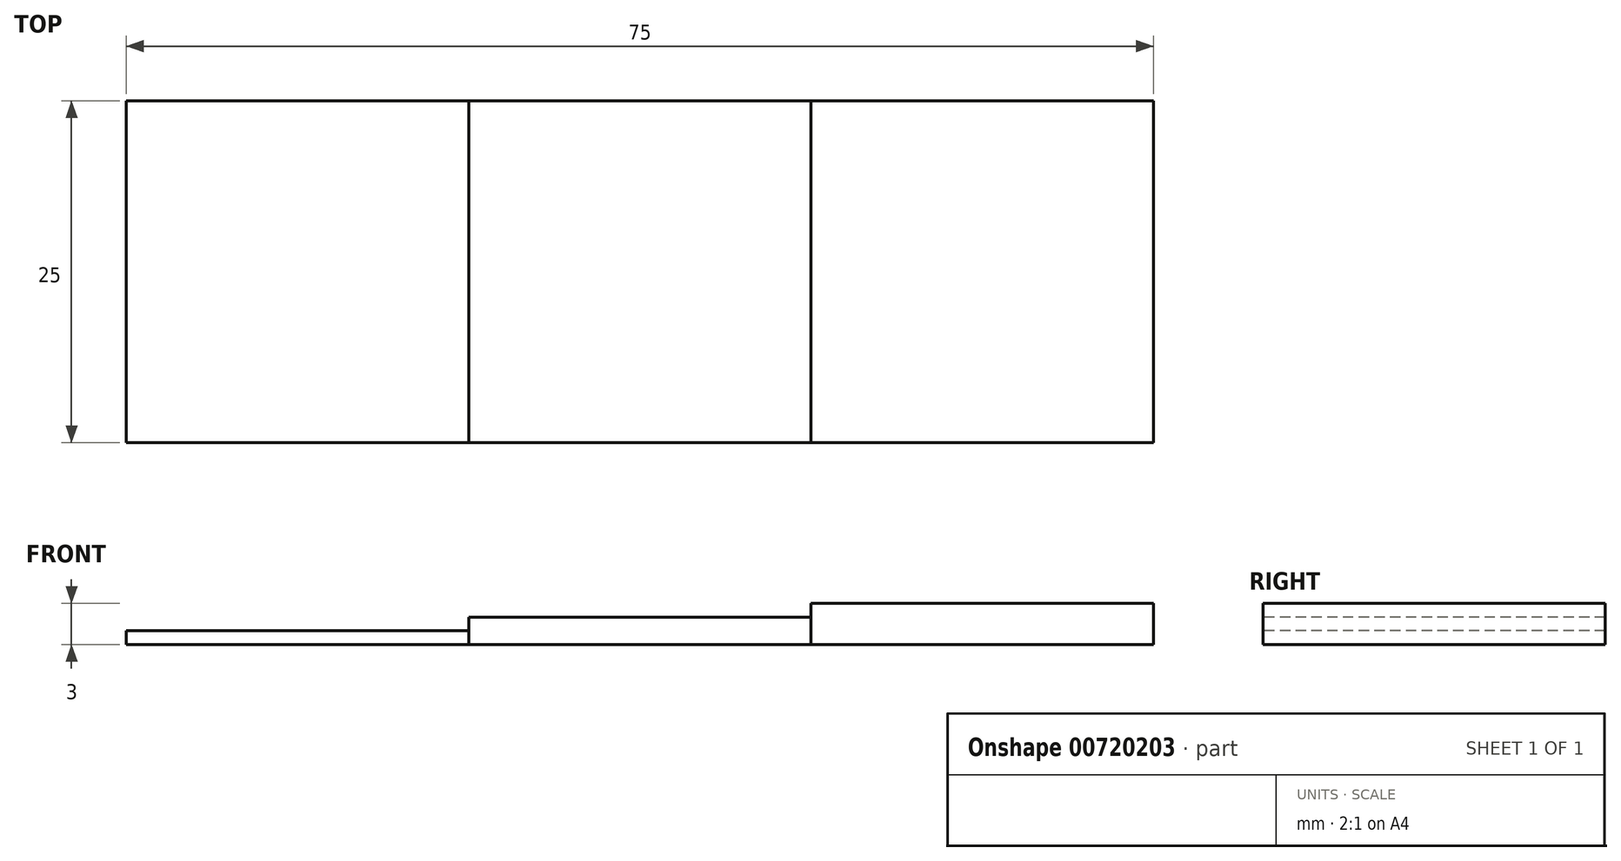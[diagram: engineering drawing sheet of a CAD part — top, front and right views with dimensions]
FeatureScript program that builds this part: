
annotation { "Feature Type Name" : "Feature", "Feature Type Description" : "" }
export const myFeature = defineFeature(function(context is Context, id is Id, definition is map)
    precondition{}
    {
        {
            var Q0;
            Q0=qCreatedBy(makeId("Top.planeOp"),FACE);
            var sketch = newSketch(context, id + "F0", { "sketchPlane" : qUnion([Q0])});
            skLineSegment(sketch, "E0.bottom", {"start": v(0, 0) * mm, "end": v(25, 0) * mm});
            skLineSegment(sketch, "E0.top", {"start": v(0, -25) * mm, "end": v(25, -25) * mm});
            skLineSegment(sketch, "E0.left", {"start": v(0, 0) * mm, "end": v(0, -25) * mm});
            skLineSegment(sketch, "E0.right", {"start": v(25, 0) * mm, "end": v(25, -25) * mm});
            skSolve(sketch);
        }
        {
            var Q0;
            Q0=makeQuery(id+"F0.imprint","IMPRINT",FACE,{"disambiguationData":[TD([[makeQuery(id+"F0.imprint","IMPRINT",EDGE,{"derivedFrom":sQuery(id+"F0.wireOp",EDGE,"E0.bottom")}),-1.0]])]});
            extrude(context, id + "F1", {"entities" : qUnion([Q0]), "depth" : 1 * mm, "offsetDistance" : 25 * mm});
        }
        {
            var Q0;
            Q0=qCreatedBy(makeId("Top.planeOp"),FACE);
            var sketch = newSketch(context, id + "F2", { "sketchPlane" : qUnion([Q0])});
            skLineSegment(sketch, "E1.bottom", {"start": v(25.05, 0) * mm, "end": v(50.05, 0) * mm});
            skLineSegment(sketch, "E1.top", {"start": v(25.05, -25) * mm, "end": v(50.05, -25) * mm});
            skLineSegment(sketch, "E1.left", {"start": v(25.05, 0) * mm, "end": v(25.05, -25) * mm});
            skLineSegment(sketch, "E1.right", {"start": v(50.05, 0) * mm, "end": v(50.05, -25) * mm});
            skSolve(sketch);
        }
        {
            var Q0;
            Q0=makeQuery(id+"F2.imprint","IMPRINT",FACE,{"disambiguationData":[TD([[makeQuery(id+"F2.imprint","IMPRINT",EDGE,{"derivedFrom":sQuery(id+"F2.wireOp",EDGE,"E1.bottom")}),-1.0]])]});
            extrude(context, id + "F3", {"entities" : qUnion([Q0]), "depth" : 2 * mm, "offsetDistance" : 25 * mm});
        }
        {
            var Q0;
            Q0=makeQuery(id+"F3.opExtrude","CAP_FACE",FACE,{"disambiguationData":[OSD([sQuery(id+"F2.wireOp",EDGE,"E1.bottom"),sQuery(id+"F2.wireOp",EDGE,"E1.top"),sQuery(id+"F2.wireOp",EDGE,"E1.left"),sQuery(id+"F2.wireOp",EDGE,"E1.right")])],"isStart":false});
            var sketch = newSketch(context, id + "F4", { "sketchPlane" : qUnion([Q0])});
            skLineSegment(sketch, "E2.bottom", {"start": v(50.05, 0) * mm, "end": v(75.05, 0) * mm});
            skLineSegment(sketch, "E2.top", {"start": v(50.05, -25) * mm, "end": v(75.05, -25) * mm});
            skLineSegment(sketch, "E2.left", {"start": v(50.05, 0) * mm, "end": v(50.05, -25) * mm});
            skLineSegment(sketch, "E2.right", {"start": v(75.05, 0) * mm, "end": v(75.05, -25) * mm});
            skSolve(sketch);
        }
        {
            var Q0;
            Q0=makeQuery(id+"F4.imprint","IMPRINT",FACE,{"disambiguationData":[TD([[makeQuery(id+"F4.imprint","IMPRINT",EDGE,{"derivedFrom":sQuery(id+"F4.wireOp",EDGE,"E2.bottom")}),-1.0]])]});
            extrude(context, id + "F5", {"entities" : qUnion([Q0]), "depth" : 3 * mm, "offsetDistance" : 25 * mm});
        }
        {
            var Q0;
            Q0=makeQuery(id+"F5.opExtrude","SWEPT_BODY",BODY,{"disambiguationData":[OSD([sQuery(id+"F4.wireOp",EDGE,"E2.bottom"),sQuery(id+"F4.wireOp",EDGE,"E2.top"),sQuery(id+"F4.wireOp",EDGE,"E2.left"),sQuery(id+"F4.wireOp",EDGE,"E2.right")])]});
            var Q1;
            Q1=makeQuery(id+"F3.opExtrude","CAP_VERTEX",VERTEX,{"disambiguationData":[OSD([sQuery(id+"F2.wireOp",EDGE,"E1.top"),sQuery(id+"F2.wireOp",EDGE,"E1.right")])],"isStart":false});
            var Q2;
            Q2=makeQuery(id+"F3.opExtrude","CAP_VERTEX",VERTEX,{"disambiguationData":[OSD([sQuery(id+"F2.wireOp",EDGE,"E1.top"),sQuery(id+"F2.wireOp",EDGE,"E1.right")])],"isStart":true});
            transform(context, id + "F6", {"entities" : qUnion([Q0]), "transformType" : TransformType.TRANSLATION_ENTITY, "oppositeDirectionEntity" : false, "transformLine" : qUnion([Q1, Q2]), "makeCopy" : false});
        }
        {
            var Q0;
            Q0=makeQuery(id+"F1.opExtrude","SWEPT_BODY",BODY,{"disambiguationData":[OSD([sQuery(id+"F0.wireOp",EDGE,"E0.bottom"),sQuery(id+"F0.wireOp",EDGE,"E0.top"),sQuery(id+"F0.wireOp",EDGE,"E0.left"),sQuery(id+"F0.wireOp",EDGE,"E0.right")])]});
            var Q1;
            Q1=makeQuery(id+"F1.opExtrude","CAP_VERTEX",VERTEX,{"disambiguationData":[OSD([sQuery(id+"F0.wireOp",EDGE,"E0.top"),sQuery(id+"F0.wireOp",EDGE,"E0.right")])],"isStart":true});
            var Q2;
            Q2=makeQuery(id+"F3.opExtrude","CAP_VERTEX",VERTEX,{"disambiguationData":[OSD([sQuery(id+"F2.wireOp",EDGE,"E1.top"),sQuery(id+"F2.wireOp",EDGE,"E1.left")])],"isStart":true});
            transform(context, id + "F7", {"entities" : qUnion([Q0]), "transformType" : TransformType.TRANSLATION_ENTITY, "oppositeDirectionEntity" : false, "transformLine" : qUnion([Q1, Q2]), "makeCopy" : false});
        }
    });
